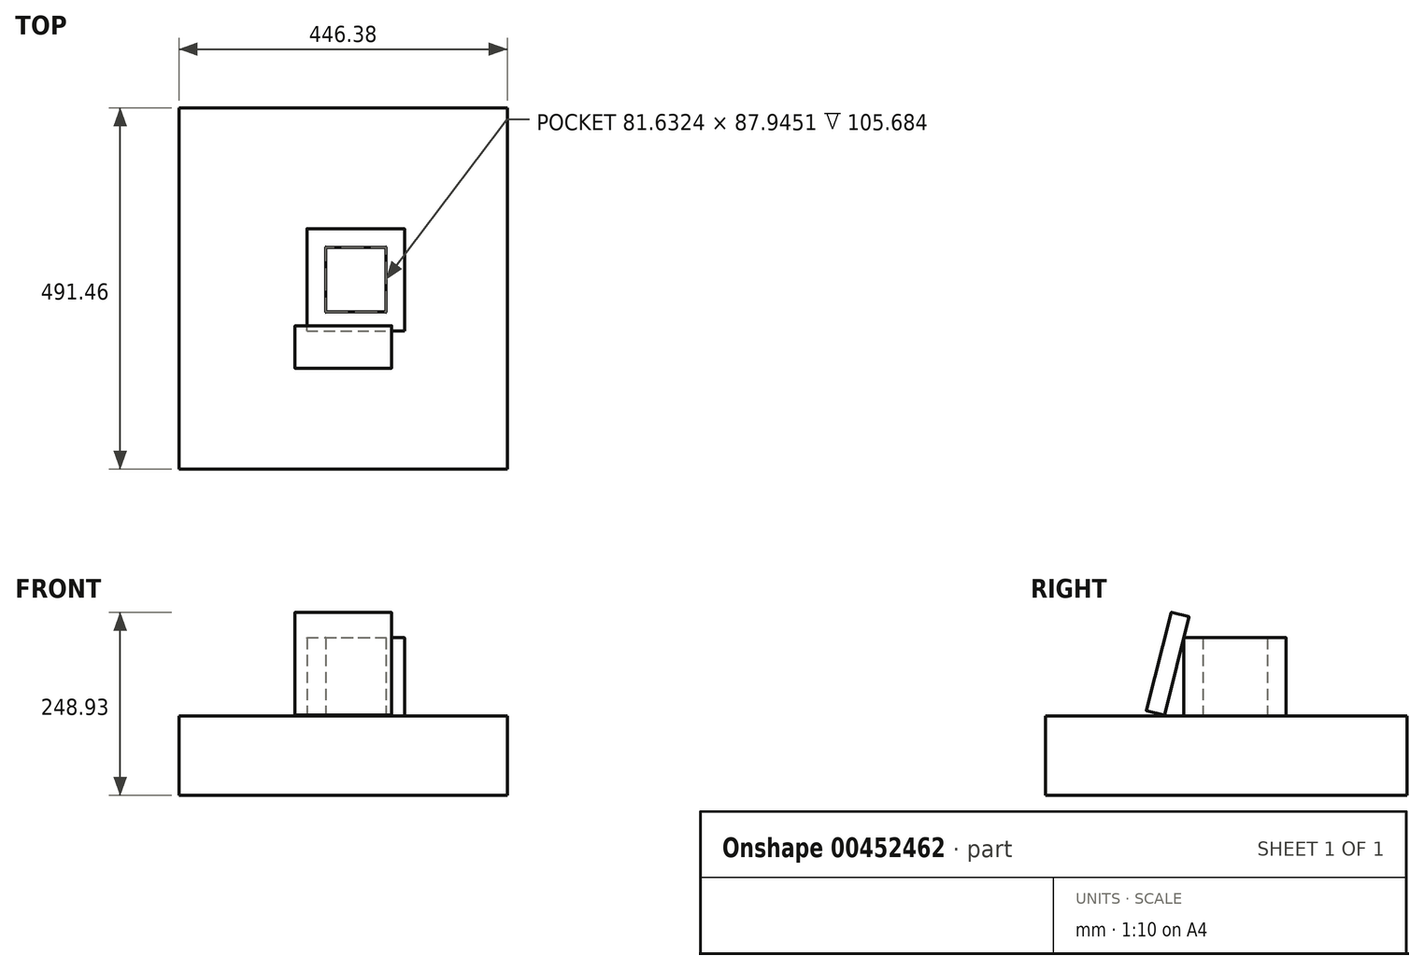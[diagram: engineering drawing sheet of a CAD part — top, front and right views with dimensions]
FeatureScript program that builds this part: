
annotation { "Feature Type Name" : "Feature", "Feature Type Description" : "" }
export const myFeature = defineFeature(function(context is Context, id is Id, definition is map)
    precondition{}
    {
        {
            var Q0;
            Q0=qCreatedBy(makeId("Top.planeOp"),FACE);
            var sketch = newSketch(context, id + "F0", { "sketchPlane" : qUnion([Q0])});
            skLineSegment(sketch, "E0.bottom", {"start": v(-58.9, -35.7) * mm, "end": v(22.74, -35.7) * mm});
            skLineSegment(sketch, "E0.top", {"start": v(-58.9, 52.24) * mm, "end": v(22.74, 52.24) * mm});
            skLineSegment(sketch, "E0.left", {"start": v(-58.9, -35.7) * mm, "end": v(-58.9, 52.24) * mm});
            skLineSegment(sketch, "E0.right", {"start": v(22.74, -35.7) * mm, "end": v(22.74, 52.24) * mm});
            skSolve(sketch);
        }
        {
            var Q0;
            Q0=makeQuery(id+"F0.imprint","IMPRINT",FACE,{"disambiguationData":[TD([[makeQuery(id+"F0.imprint","IMPRINT",EDGE,{"derivedFrom":sQuery(id+"F0.wireOp",EDGE,"E0.bottom")}),1.0]])]});
            var sketch = newSketch(context, id + "F1", { "sketchPlane" : qUnion([Q0])});
            skLineSegment(sketch, "E1.0", {"start": v(48.3, -61.28) * mm, "end": v(48.3, 77.8) * mm});
            skLineSegment(sketch, "E1.1", {"start": v(-84.46, -61.28) * mm, "end": v(48.3, -61.28) * mm});
            skLineSegment(sketch, "E1.2", {"start": v(-84.46, -61.28) * mm, "end": v(-84.46, 77.8) * mm});
            skLineSegment(sketch, "E1.3", {"start": v(-84.46, 77.8) * mm, "end": v(48.3, 77.8) * mm});
            skSolve(sketch);
        }
        {
            var Q0;
            Q0=makeQuery(id+"F1.imprint","IMPRINT",FACE,{"disambiguationData":[TD([[makeQuery(id+"F1.imprint","IMPRINT",EDGE,{"derivedFrom":sQuery(id+"F1.wireOp",EDGE,"E1.0")}),1.0]])]});
            extrude(context, id + "F2", {"entities" : qUnion([Q0]), "depth" : 106.2 * mm});
        }
        {
            var Q0;
            Q0=makeQuery(id+"F2.opExtrude","CAP_FACE",FACE,{"disambiguationData":[OSD([sQuery(id+"F0.wireOp",EDGE,"E0.bottom"),sQuery(id+"F0.wireOp",EDGE,"E0.top"),sQuery(id+"F0.wireOp",EDGE,"E0.left"),sQuery(id+"F0.wireOp",EDGE,"E0.right"),sQuery(id+"F1.wireOp",EDGE,"E1.0"),sQuery(id+"F1.wireOp",EDGE,"E1.1"),sQuery(id+"F1.wireOp",EDGE,"E1.2"),sQuery(id+"F1.wireOp",EDGE,"E1.3")])],"isStart":false});
            fillet(context, id + "F3", {"entities" : qUnion([Q0]), "radius" : 0.5 * mm, "tangentPropagation" : true, "allowEdgeOverflow" : false});
        }
        {
            var Q0;
            Q0=makeQuery(id+"F2.opExtrude","CAP_FACE",FACE,{"disambiguationData":[OSD([sQuery(id+"F0.wireOp",EDGE,"E0.bottom"),sQuery(id+"F0.wireOp",EDGE,"E0.top"),sQuery(id+"F0.wireOp",EDGE,"E0.left"),sQuery(id+"F0.wireOp",EDGE,"E0.right"),sQuery(id+"F1.wireOp",EDGE,"E1.0"),sQuery(id+"F1.wireOp",EDGE,"E1.1"),sQuery(id+"F1.wireOp",EDGE,"E1.2"),sQuery(id+"F1.wireOp",EDGE,"E1.3")])],"isStart":false});
            var sketch = newSketch(context, id + "F4", { "sketchPlane" : qUnion([Q0])});
            skLineSegment(sketch, "E2.bottom", {"start": v(-83.96, 77.3) * mm, "end": v(47.8, 77.3) * mm});
            skLineSegment(sketch, "E2.top", {"start": v(-83.96, -60.77) * mm, "end": v(47.8, -60.77) * mm});
            skLineSegment(sketch, "E2.left", {"start": v(-83.96, 77.3) * mm, "end": v(-83.96, -60.77) * mm});
            skLineSegment(sketch, "E2.right", {"start": v(47.8, 77.3) * mm, "end": v(47.8, -60.77) * mm});
            skSolve(sketch);
        }
        {
            var Q0;
            Q0=makeQuery(id+"F4.imprint","IMPRINT",FACE,{"disambiguationData":[TD([[makeQuery(id+"F4.imprint","IMPRINT",EDGE,{"derivedFrom":sQuery(id+"F4.wireOp",EDGE,"E2.bottom")}),1.0]])]});
            var Q1;
            {var subQ0=sQuery(id+"F0.wireOp",EDGE,"E0.right");var subQ1=sQuery(id+"F0.wireOp",EDGE,"E0.left");var subQ2=sQuery(id+"F0.wireOp",EDGE,"E0.top");var subQ3=sQuery(id+"F0.wireOp",EDGE,"E0.bottom");var subQ4=makeQuery(id+"F2.opExtrude","CAP_FACE",FACE,{"disambiguationData":[OSD([subQ3,subQ2,subQ1,subQ0,sQuery(id+"F1.wireOp",EDGE,"E1.0"),sQuery(id+"F1.wireOp",EDGE,"E1.1"),sQuery(id+"F1.wireOp",EDGE,"E1.2"),sQuery(id+"F1.wireOp",EDGE,"E1.3")])],"isStart":false});Q1=makeQuery(id+"F4.imprint","IMPRINT",FACE,{"disambiguationData":[TD([[makeQuery(id+"F4.imprint","IMPRINT",EDGE,{"derivedFrom":makeQuery(id+"F3.opFillet","BLEND_EDGE",EDGE,{"blendedFrom":[makeQuery(id+"F2.opExtrude","CAP_EDGE",EDGE,{"disambiguationData":[OSD([subQ3])],"isStart":false}),subQ4],"blendedInto":[subQ4]})}),-1.0]])]});}
            var Q2;
            Q2=sQuery(id+"F4.wireOp",EDGE,"E2.top");
            var Q3;
            Q3=sQuery(id+"F4.wireOp",EDGE,"E2.left");
            var Q4;
            Q4=sQuery(id+"F4.wireOp",EDGE,"E2.bottom");
            var Q5;
            Q5=sQuery(id+"F4.wireOp",EDGE,"E2.right");
            extrude(context, id + "F5", {"entities" : qUnion([Q0, Q1]), "surfaceEntities" : qUnion([Q2, Q3, Q4, Q5]), "depth" : 25.4 * mm});
        }
        {
            var Q0;
            Q0=makeQuery(id+"F5.opExtrude","CAP_FACE",FACE,{"disambiguationData":[OSD([sQuery(id+"F4.wireOp",EDGE,"E2.bottom"),sQuery(id+"F4.wireOp",EDGE,"E2.top"),sQuery(id+"F4.wireOp",EDGE,"E2.left"),sQuery(id+"F4.wireOp",EDGE,"E2.right")])],"isStart":false});
            var Q1;
            Q1=makeQuery(id+"F5.opExtrude","CAP_FACE",FACE,{"disambiguationData":[OSD([sQuery(id+"F4.wireOp",EDGE,"E2.bottom"),sQuery(id+"F4.wireOp",EDGE,"E2.top"),sQuery(id+"F4.wireOp",EDGE,"E2.left"),sQuery(id+"F4.wireOp",EDGE,"E2.right")])],"isStart":true});
            fillet(context, id + "F6", {"entities" : qUnion([Q0, Q1]), "radius" : 0.5 * mm, "tangentPropagation" : true, "allowEdgeOverflow" : false});
        }
        {
            var Q0;
            Q0=makeQuery(id+"F5.opExtrude","SWEPT_BODY",BODY,{"disambiguationData":[OSD([sQuery(id+"F4.wireOp",EDGE,"E2.bottom"),sQuery(id+"F4.wireOp",EDGE,"E2.top"),sQuery(id+"F4.wireOp",EDGE,"E2.left"),sQuery(id+"F4.wireOp",EDGE,"E2.right")])]});
            var Q1;
            Q1=sQuery(id+"F4.wireOp",EDGE,"E2.top");
            transform(context, id + "F7", {"entities" : qUnion([Q0]), "transformType" : TransformType.ROTATION, "transformAxis" : qUnion([Q1]), "angle" : 76 * degree, "makeCopy" : false});
        }
        {
            var Q0;
            Q0=makeQuery(id+"F5.opExtrude","SWEPT_BODY",BODY,{"disambiguationData":[OSD([sQuery(id+"F4.wireOp",EDGE,"E2.bottom"),sQuery(id+"F4.wireOp",EDGE,"E2.top"),sQuery(id+"F4.wireOp",EDGE,"E2.left"),sQuery(id+"F4.wireOp",EDGE,"E2.right")])]});
            var Q1;
            Q1=qCreatedBy(makeId("Top.planeOp"),FACE);
            transform(context, id + "F8", {"entities" : qUnion([Q0]), "transformType" : TransformType.TRANSLATION_DISTANCE, "transformDirection" : qUnion([Q1]), "distance" : 104.14 * mm, "oppositeDirection" : true, "makeCopy" : false});
        }
        {
            var Q0;
            Q0=makeQuery(id+"F5.opExtrude","SWEPT_BODY",BODY,{"disambiguationData":[OSD([sQuery(id+"F4.wireOp",EDGE,"E2.bottom"),sQuery(id+"F4.wireOp",EDGE,"E2.top"),sQuery(id+"F4.wireOp",EDGE,"E2.left"),sQuery(id+"F4.wireOp",EDGE,"E2.right")])]});
            transform(context, id + "F9", {"entities" : qUnion([Q0]), "transformType" : TransformType.TRANSLATION_3D, "dx" : -16.97 * mm, "dy" : -26.8 * mm, "dz" : -1.33 * mm, "makeCopy" : false});
        }
        {
            var Q0;
            Q0=qCreatedBy(makeId("Top.planeOp"),FACE);
            var sketch = newSketch(context, id + "F10", { "sketchPlane" : qUnion([Q0])});
            skLineSegment(sketch, "E3.bottom", {"start": v(187.96, -249.48) * mm, "end": v(-258.42, -249.48) * mm});
            skLineSegment(sketch, "E3.top", {"start": v(187.96, 241.98) * mm, "end": v(-258.42, 241.98) * mm});
            skLineSegment(sketch, "E3.left", {"start": v(187.96, -249.48) * mm, "end": v(187.96, 241.98) * mm});
            skLineSegment(sketch, "E3.right", {"start": v(-258.42, -249.48) * mm, "end": v(-258.42, 241.98) * mm});
            skSolve(sketch);
        }
        {
            var Q0;
            Q0=makeQuery(id+"F10.imprint","IMPRINT",FACE,{"disambiguationData":[TD([[makeQuery(id+"F10.imprint","IMPRINT",EDGE,{"derivedFrom":sQuery(id+"F10.wireOp",EDGE,"E3.bottom")}),-1.0]])]});
            extrude(context, id + "F11", {"entities" : qUnion([Q0]), "operationType" : NewBodyOperationType.ADD, "oppositeDirection" : true, "depth" : 2.54 * mm, "offsetDistance" : 25.4 * mm});
        }
        {
            var Q0;
            Q0=makeQuery(id+"F11.opExtrude","CAP_FACE",FACE,{"disambiguationData":[OSD([sQuery(id+"F10.wireOp",EDGE,"E3.bottom"),sQuery(id+"F10.wireOp",EDGE,"E3.top"),sQuery(id+"F10.wireOp",EDGE,"E3.left"),sQuery(id+"F10.wireOp",EDGE,"E3.right")])],"isStart":false});
            extrude(context, id + "F12", {"entities" : qUnion([Q0]), "operationType" : NewBodyOperationType.ADD, "depth" : 105.66 * mm, "offsetDistance" : 25.4 * mm});
        }
    });
